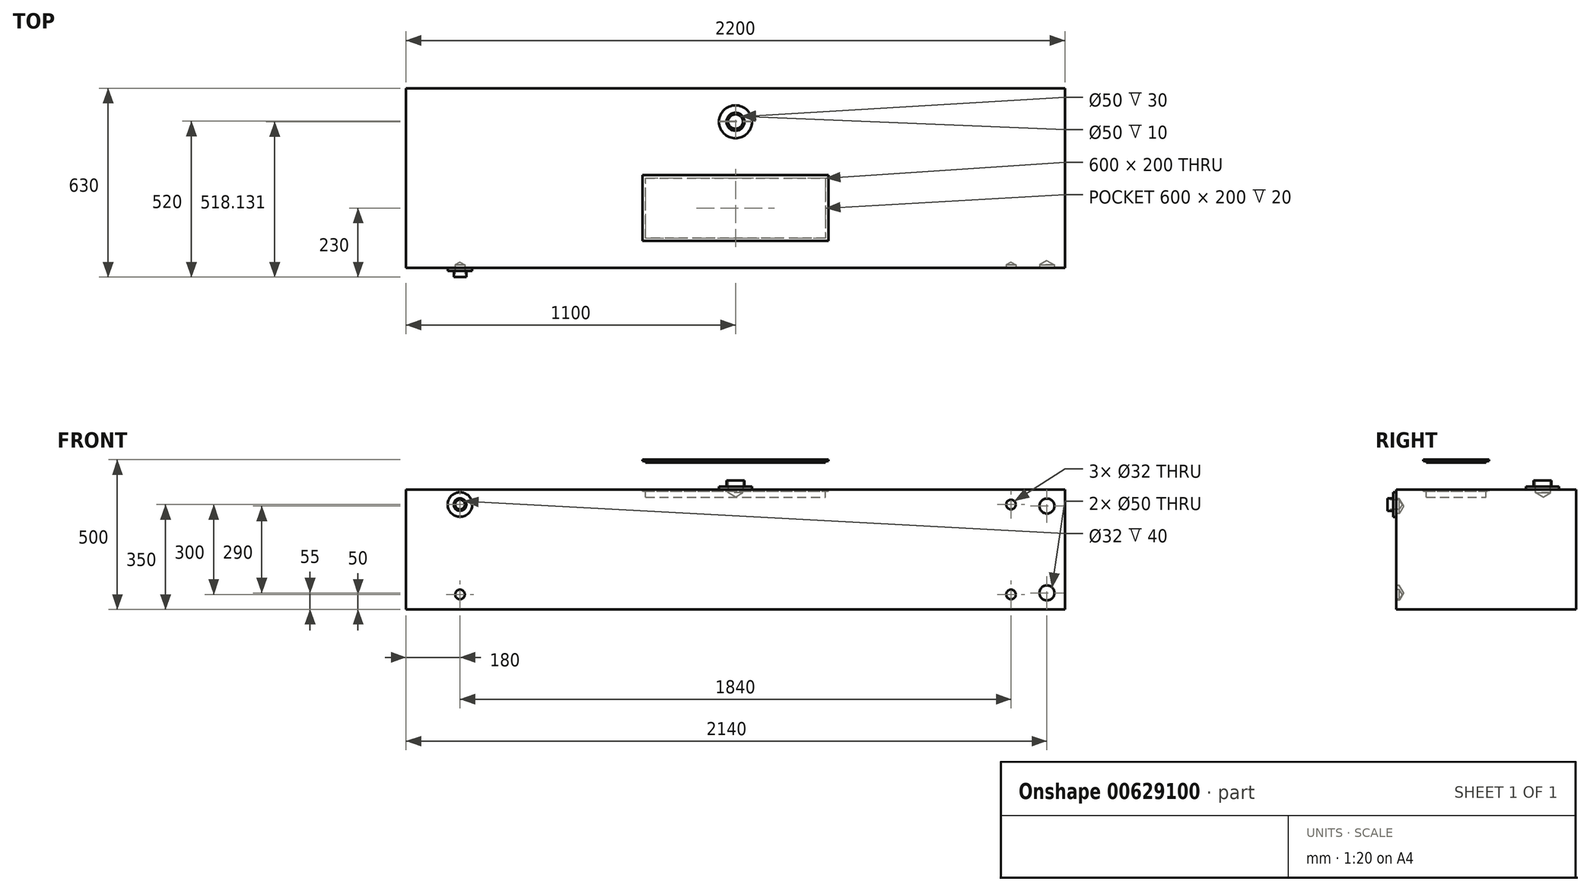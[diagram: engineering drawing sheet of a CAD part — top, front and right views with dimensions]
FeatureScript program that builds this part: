
annotation { "Feature Type Name" : "Feature", "Feature Type Description" : "" }
export const myFeature = defineFeature(function(context is Context, id is Id, definition is map)
    precondition{}
    {
        {
            var Q0;
            Q0=qCreatedBy(makeId("Top.planeOp"),FACE);
            var sketch = newSketch(context, id + "F0", { "sketchPlane" : qUnion([Q0])});
            skLineSegment(sketch, "E0.bottom", {"start": v(1100, -300) * mm, "end": v(-1100, -300) * mm});
            skLineSegment(sketch, "E0.top", {"start": v(1100, 300) * mm, "end": v(-1100, 300) * mm});
            skLineSegment(sketch, "E0.left", {"start": v(1100, -300) * mm, "end": v(1100, 300) * mm});
            skLineSegment(sketch, "E0.right", {"start": v(-1100, -300) * mm, "end": v(-1100, 300) * mm});
            skPoint(sketch, "E0.middle", {"position": v(0, 0) * mm});
            skPoint(sketch, "E1", {"position": v(0, -300) * mm});
            skPoint(sketch, "E2", {"position": v(0, 300) * mm});
            skPoint(sketch, "E3", {"position": v(-520, -300) * mm});
            skPoint(sketch, "E4", {"position": v(520, -300) * mm});
            skPoint(sketch, "E5", {"position": v(1100, 0) * mm});
            skPoint(sketch, "E6", {"position": v(-1100, 0) * mm});
            skLineSegment(sketch, "E7", {"start": v(-300, 0) * mm, "end": v(300, 0) * mm});
            skLineSegment(sketch, "E8", {"start": v(300, 0) * mm, "end": v(300, -200) * mm});
            skLineSegment(sketch, "E9", {"start": v(300, -200) * mm, "end": v(-300, -200) * mm});
            skLineSegment(sketch, "E10", {"start": v(-300, -200) * mm, "end": v(-300, 0) * mm});
            skLineSegment(sketch, "E11.0", {"start": v(-310, 10) * mm, "end": v(310, 10) * mm});
            skLineSegment(sketch, "E11.1", {"start": v(-310, -210) * mm, "end": v(-310, 10) * mm});
            skLineSegment(sketch, "E11.2", {"start": v(310, -210) * mm, "end": v(-310, -210) * mm});
            skLineSegment(sketch, "E11.3", {"start": v(310, 10) * mm, "end": v(310, -210) * mm});
            skPoint(sketch, "E12", {"position": v(0, 190) * mm});
            skSolve(sketch);
        }
        {
            var Q0;
            Q0=makeQuery(id+"F0.imprint","IMPRINT",FACE,{"disambiguationData":[TD([[makeQuery(id+"F0.imprint","IMPRINT",EDGE,{"derivedFrom":sQuery(id+"F0.wireOp",EDGE,"E0.bottom")}),-1.0]])]});
            var Q1;
            Q1=makeQuery(id+"F0.imprint","IMPRINT",FACE,{"disambiguationData":[TD([[makeQuery(id+"F0.imprint","IMPRINT",EDGE,{"derivedFrom":sQuery(id+"F0.wireOp",EDGE,"E7")}),-1.0]])]});
            var Q2;
            Q2=makeQuery(id+"F0.imprint","IMPRINT",FACE,{"disambiguationData":[TD([[makeQuery(id+"F0.imprint","IMPRINT",EDGE,{"derivedFrom":sQuery(id+"F0.wireOp",EDGE,"E7")}),1.0]])]});
            extrude(context, id + "F1", {"entities" : qUnion([Q0, Q1, Q2]), "oppositeDirection" : true, "depth" : 400 * mm, "offsetDistance" : 25 * mm});
        }
        {
            var Q0;
            Q0=sQuery(id+"F0.wireOp",VERTEX,"E12");
            var Q1;
            Q1=makeQuery(id+"F1.opExtrude","SWEPT_BODY",BODY,{"disambiguationData":[OSD([sQuery(id+"F0.wireOp",EDGE,"E0.bottom"),sQuery(id+"F0.wireOp",EDGE,"E0.top"),sQuery(id+"F0.wireOp",EDGE,"E0.left"),sQuery(id+"F0.wireOp",EDGE,"E0.right")])]});
            hole(context, id + "F2", {"style" : HoleStyle.SIMPLE, "endStyle" : HoleEndStyle.BLIND, "holeDiameter" : 50 * mm, "majorDiameter" : 5 * mm, "holeDepth" : 10 * mm, "isTappedThrough" : true, "tappedDepth" : 12 * mm, "tapClearance" : 3, "locations" : qUnion([Q0]), "scope" : qUnion([Q1])});
        }
        {
            var Q0;
            Q0=makeQuery(id+"F0.imprint","IMPRINT",FACE,{"disambiguationData":[TD([[makeQuery(id+"F0.imprint","IMPRINT",EDGE,{"derivedFrom":sQuery(id+"F0.wireOp",EDGE,"E7")}),-1.0]])]});
            extrude(context, id + "F3", {"entities" : qUnion([Q0]), "operationType" : NewBodyOperationType.REMOVE, "oppositeDirection" : true, "depth" : 25 * mm, "offsetDistance" : 25 * mm});
        }
        {
            var Q0;
            Q0=makeQuery(id+"F0.imprint","IMPRINT",FACE,{"disambiguationData":[TD([[makeQuery(id+"F0.imprint","IMPRINT",EDGE,{"derivedFrom":sQuery(id+"F0.wireOp",EDGE,"E7")}),1.0]])]});
            extrude(context, id + "F4", {"entities" : qUnion([Q0]), "operationType" : NewBodyOperationType.REMOVE, "oppositeDirection" : true, "depth" : 5 * mm, "offsetDistance" : 25 * mm});
        }
        {
            var Q0;
            Q0=makeQuery(id+"F1.opExtrude","SWEPT_FACE",FACE,{"disambiguationData":[OSD([sQuery(id+"F0.wireOp",EDGE,"E0.bottom")])]});
            var sketch = newSketch(context, id + "F5", { "sketchPlane" : qUnion([Q0])});
            skPoint(sketch, "E13", {"position": v(-920, -350) * mm});
            skPoint(sketch, "E14.MirrorP", {"position": v(920, -350) * mm});
            skPoint(sketch, "E15", {"position": v(-920, -50) * mm});
            skPoint(sketch, "E16.MirrorP", {"position": v(920, -50) * mm});
            skPoint(sketch, "E17", {"position": v(1040, -55) * mm});
            skPoint(sketch, "E18", {"position": v(1100, -200) * mm});
            skPoint(sketch, "E19", {"position": v(1040, -345) * mm});
            skSolve(sketch);
        }
        {
            var Q0;
            Q0=sQuery(id+"F5.wireOp",VERTEX,"E13");
            var Q1;
            Q1=sQuery(id+"F5.wireOp",VERTEX,"E15");
            var Q2;
            Q2=sQuery(id+"F5.wireOp",VERTEX,"E16.MirrorP");
            var Q3;
            Q3=sQuery(id+"F5.wireOp",VERTEX,"E14.MirrorP");
            var Q4;
            Q4=makeQuery(id+"F1.opExtrude","SWEPT_BODY",BODY,{"disambiguationData":[OSD([sQuery(id+"F0.wireOp",EDGE,"E0.bottom"),sQuery(id+"F0.wireOp",EDGE,"E0.top"),sQuery(id+"F0.wireOp",EDGE,"E0.left"),sQuery(id+"F0.wireOp",EDGE,"E0.right")])]});
            hole(context, id + "F6", {"style" : HoleStyle.SIMPLE, "endStyle" : HoleEndStyle.BLIND, "holeDiameter" : 32 * mm, "majorDiameter" : 5 * mm, "holeDepth" : 10 * mm, "isTappedThrough" : true, "tappedDepth" : 12 * mm, "tapClearance" : 3, "locations" : qUnion([Q0, Q1, Q2, Q3]), "scope" : qUnion([Q4])});
        }
        {
            var Q0;
            Q0=makeQuery(id+"F0.imprint","IMPRINT",FACE,{"disambiguationData":[TD([[makeQuery(id+"F0.imprint","IMPRINT",EDGE,{"derivedFrom":sQuery(id+"F0.wireOp",EDGE,"E0.bottom")}),-1.0]])]});
            var sketch = newSketch(context, id + "F7", { "sketchPlane" : qUnion([Q0])});
            skCircle(sketch, "E20.0", {"center": v(0, 188.13) * mm, "radius": 25 * mm});
            skCircle(sketch, "E21.0", {"center": v(0, 188.13) * mm, "radius": 30 * mm});
            skCircle(sketch, "E22.0", {"center": v(0, 188.13) * mm, "radius": 55 * mm});
            skSolve(sketch);
        }
        {
            var Q0;
            Q0=makeQuery(id+"F7.imprint","IMPRINT",FACE,{"disambiguationData":[TD([[makeQuery(id+"F7.imprint","IMPRINT",EDGE,{"derivedFrom":sQuery(id+"F7.wireOp",EDGE,"E20.0")}),-1.0]])]});
            extrude(context, id + "F8", {"entities" : qUnion([Q0]), "depth" : 30 * mm, "offsetDistance" : 25 * mm});
        }
        {
            var Q0;
            Q0=makeQuery(id+"F7.imprint","IMPRINT",FACE,{"disambiguationData":[TD([[makeQuery(id+"F7.imprint","IMPRINT",EDGE,{"derivedFrom":sQuery(id+"F7.wireOp",EDGE,"E21.0")}),-1.0]])]});
            extrude(context, id + "F9", {"entities" : qUnion([Q0]), "operationType" : NewBodyOperationType.ADD, "depth" : 10 * mm, "offsetDistance" : 25 * mm});
        }
        {
            var Q0;
            {var subQ0=sQuery(id+"F0.wireOp",EDGE,"E0.bottom");Q0=makeQuery(id+"F5.imprint","IMPRINT",FACE,{"disambiguationData":[TD([[makeQuery(id+"F5.imprint","IMPRINT",EDGE,{"derivedFrom":makeQuery(id+"F1.opExtrude","CAP_EDGE",EDGE,{"disambiguationData":[OSD([subQ0])],"isStart":true})}),1.0]])]});}
            var sketch = newSketch(context, id + "F10", { "sketchPlane" : qUnion([Q0])});
            skCircle(sketch, "E23.0", {"center": v(-920, -50) * mm, "radius": 16 * mm});
            skCircle(sketch, "E24.0", {"center": v(-920, -50) * mm, "radius": 21 * mm});
            skCircle(sketch, "E25.0", {"center": v(-920, -50) * mm, "radius": 41 * mm});
            skSolve(sketch);
        }
        {
            var Q0;
            Q0=makeQuery(id+"F10.imprint","IMPRINT",FACE,{"disambiguationData":[TD([[makeQuery(id+"F10.imprint","IMPRINT",EDGE,{"derivedFrom":sQuery(id+"F10.wireOp",EDGE,"E23.0")}),-1.0]])]});
            extrude(context, id + "F11", {"entities" : qUnion([Q0]), "depth" : 30 * mm, "offsetDistance" : 25 * mm});
        }
        {
            var Q0;
            Q0=qSketchRegion(id+"F10",true);
            extrude(context, id + "F12", {"entities" : qUnion([Q0]), "operationType" : NewBodyOperationType.ADD, "depth" : 10 * mm, "offsetDistance" : 25 * mm});
        }
        {
            var Q0;
            Q0=sQuery(id+"F5.wireOp",VERTEX,"E17");
            var Q1;
            Q1=sQuery(id+"F5.wireOp",VERTEX,"E19");
            var Q2;
            Q2=makeQuery(id+"F1.opExtrude","SWEPT_BODY",BODY,{"disambiguationData":[OSD([sQuery(id+"F0.wireOp",EDGE,"E0.bottom"),sQuery(id+"F0.wireOp",EDGE,"E0.top"),sQuery(id+"F0.wireOp",EDGE,"E0.left"),sQuery(id+"F0.wireOp",EDGE,"E0.right")])]});
            hole(context, id + "F13", {"style" : HoleStyle.SIMPLE, "endStyle" : HoleEndStyle.BLIND, "holeDiameter" : 50 * mm, "majorDiameter" : 5 * mm, "holeDepth" : 10 * mm, "isTappedThrough" : true, "tappedDepth" : 12 * mm, "tapClearance" : 3, "locations" : qUnion([Q0, Q1]), "scope" : qUnion([Q2])});
        }
        {
            var Q0;
            Q0=makeQuery(id+"F7.imprint","IMPRINT",FACE,{"disambiguationData":[TD([[makeQuery(id+"F7.imprint","IMPRINT",EDGE,{"derivedFrom":sQuery(id+"F7.wireOp",EDGE,"E22.0")}),-1.0]])]});
            cPlane(context, id + "F14", {"entities" : qUnion([Q0]), "cplaneType" : CPlaneType.OFFSET, "offset" : 100 * mm, "width" : 150 * mm, "height" : 150 * mm});
        }
        {
            var Q0;
            Q0=qCreatedBy(id+"F14.planeOp",FACE);
            var sketch = newSketch(context, id + "F15", { "sketchPlane" : qUnion([Q0])});
            skLineSegment(sketch, "E26.0", {"start": v(-310, 10) * mm, "end": v(310, 10) * mm});
            skLineSegment(sketch, "E26.1", {"start": v(310, 10) * mm, "end": v(310, -210) * mm});
            skLineSegment(sketch, "E26.2", {"start": v(310, -210) * mm, "end": v(-310, -210) * mm});
            skLineSegment(sketch, "E26.3", {"start": v(-310, -210) * mm, "end": v(-310, 10) * mm});
            skLineSegment(sketch, "E26.4", {"start": v(-300, -200) * mm, "end": v(-300, 0) * mm});
            skLineSegment(sketch, "E26.5", {"start": v(-300, 0) * mm, "end": v(300, 0) * mm});
            skLineSegment(sketch, "E26.6", {"start": v(300, 0) * mm, "end": v(300, -200) * mm});
            skLineSegment(sketch, "E26.7", {"start": v(300, -200) * mm, "end": v(-300, -200) * mm});
            skSolve(sketch);
        }
        {
            var Q0;
            Q0=makeQuery(id+"F15.imprint","IMPRINT",FACE,{"disambiguationData":[TD([[makeQuery(id+"F15.imprint","IMPRINT",EDGE,{"derivedFrom":sQuery(id+"F15.wireOp",EDGE,"E26.4")}),-1.0]])]});
            extrude(context, id + "F16", {"entities" : qUnion([Q0]), "oppositeDirection" : true, "depth" : 10 * mm, "offsetDistance" : 25 * mm});
        }
        {
            var Q0;
            Q0=makeQuery(id+"F15.imprint","IMPRINT",FACE,{"disambiguationData":[TD([[makeQuery(id+"F15.imprint","IMPRINT",EDGE,{"derivedFrom":sQuery(id+"F15.wireOp",EDGE,"E26.0")}),-1.0]])]});
            extrude(context, id + "F17", {"entities" : qUnion([Q0]), "operationType" : NewBodyOperationType.ADD, "oppositeDirection" : true, "depth" : 5 * mm, "offsetDistance" : 25 * mm});
        }
    });
